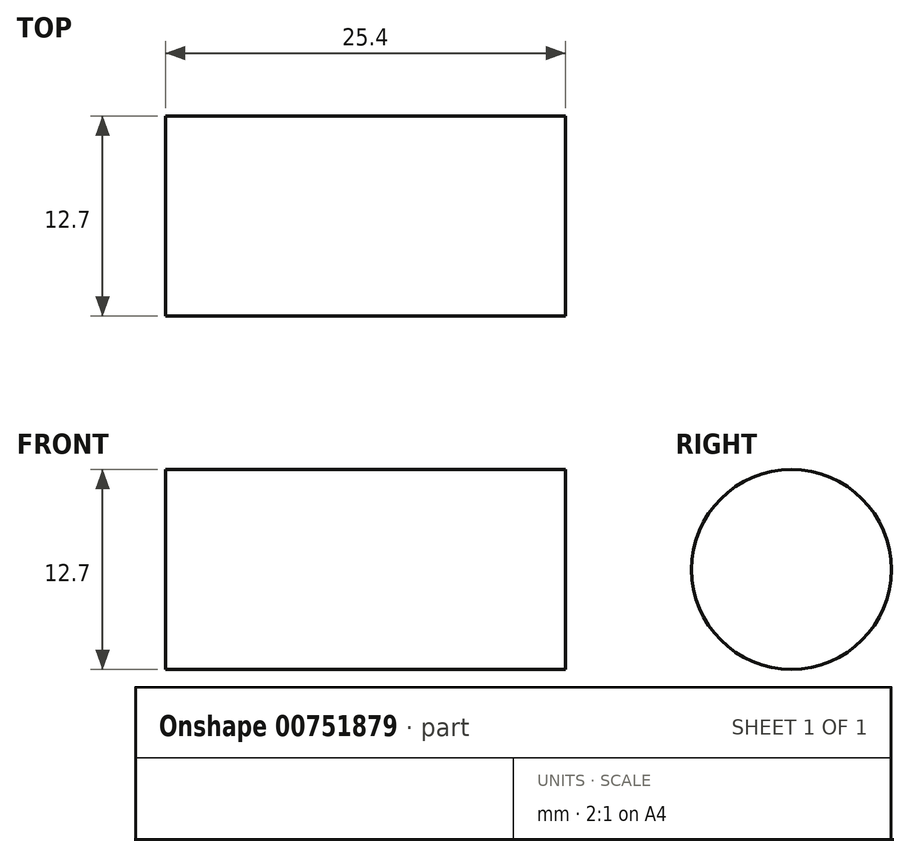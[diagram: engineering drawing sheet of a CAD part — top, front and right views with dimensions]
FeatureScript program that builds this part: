
annotation { "Feature Type Name" : "Feature", "Feature Type Description" : "" }
export const myFeature = defineFeature(function(context is Context, id is Id, definition is map)
    precondition{}
    {
        {
            var Q0;
            Q0=qCreatedBy(makeId("Right.planeOp"),FACE);
            var sketch = newSketch(context, id + "F0", { "sketchPlane" : qUnion([Q0])});
            skCircle(sketch, "E0", {"center": v(0, 0) * mm, "radius": 6.35 * mm});
            skSolve(sketch);
        }
        {
            var Q0;
            Q0=makeQuery(id+"F0.imprint","IMPRINT",FACE,{"disambiguationData":[TD([[makeQuery(id+"F0.imprint","IMPRINT",EDGE,{"derivedFrom":sQuery(id+"F0.wireOp",EDGE,"E0")}),1.0]])]});
            extrude(context, id + "F1", {"entities" : qUnion([Q0]), "depth" : 25.4 * mm, "offsetDistance" : 25.4 * mm});
        }
    });
